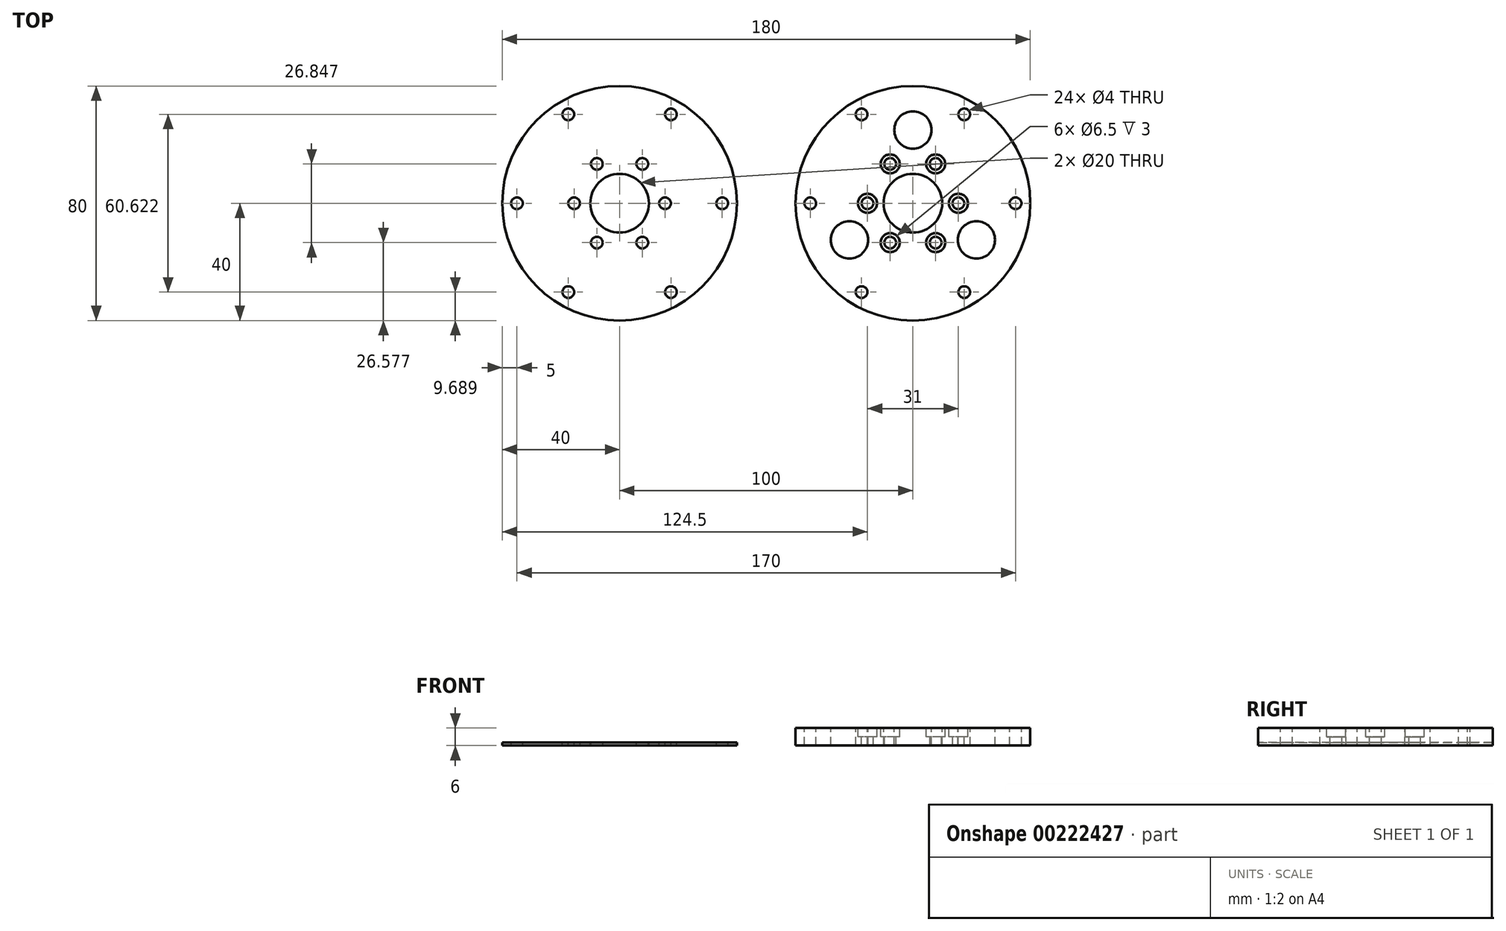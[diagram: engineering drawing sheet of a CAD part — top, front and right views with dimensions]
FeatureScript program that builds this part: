
annotation { "Feature Type Name" : "Feature", "Feature Type Description" : "" }
export const myFeature = defineFeature(function(context is Context, id is Id, definition is map)
    precondition{}
    {
        {
            var Q0;
            Q0=qCreatedBy(makeId("Top.planeOp"),FACE);
            var sketch = newSketch(context, id + "F0", { "sketchPlane" : qUnion([Q0])});
            skCircle(sketch, "E0", {"center": v(0, 0) * mm, "radius": 30 * mm});
            skCircle(sketch, "E1", {"center": v(0, 0) * mm, "radius": 40 * mm});
            skPoint(sketch, "E2", {"position": v(15.5, 0) * mm});
            skPoint(sketch, "E3.1.0", {"position": v(7.75, 13.42) * mm});
            skPoint(sketch, "E3.2.0", {"position": v(-7.75, 13.42) * mm});
            skPoint(sketch, "E3.3.0", {"position": v(-15.5, 0) * mm});
            skPoint(sketch, "E3.4.0", {"position": v(-7.75, -13.42) * mm});
            skPoint(sketch, "E3.5.0", {"position": v(7.75, -13.42) * mm});
            skPoint(sketch, "E4", {"position": v(35, 0) * mm});
            skPoint(sketch, "E5.1.0", {"position": v(17.5, 30.31) * mm});
            skPoint(sketch, "E5.2.0", {"position": v(-17.5, 30.31) * mm});
            skPoint(sketch, "E5.3.0", {"position": v(-35, 0) * mm});
            skPoint(sketch, "E5.4.0", {"position": v(-17.5, -30.31) * mm});
            skPoint(sketch, "E5.5.0", {"position": v(17.5, -30.31) * mm});
            skSolve(sketch);
        }
        {
            var Q0;
            Q0=makeQuery(id+"F0.imprint","IMPRINT",FACE,{"disambiguationData":[TD([[makeQuery(id+"F0.imprint","IMPRINT",EDGE,{"derivedFrom":sQuery(id+"F0.wireOp",EDGE,"E0")}),-1.0]])]});
            var Q1;
            Q1=makeQuery(id+"F0.imprint","IMPRINT",FACE,{"disambiguationData":[TD([[makeQuery(id+"F0.imprint","IMPRINT",EDGE,{"derivedFrom":sQuery(id+"F0.wireOp",EDGE,"E0")}),1.0]])]});
            extrude(context, id + "F1", {"entities" : qUnion([Q0, Q1]), "oppositeDirection" : true, "depth" : 1 * mm});
        }
        {
            var Q0;
            Q0=sQuery(id+"F0.wireOp",VERTEX,"E4");
            var Q1;
            Q1=sQuery(id+"F0.wireOp",VERTEX,"E5.1.0");
            var Q2;
            Q2=sQuery(id+"F0.wireOp",VERTEX,"E5.2.0");
            var Q3;
            Q3=sQuery(id+"F0.wireOp",VERTEX,"E5.3.0");
            var Q4;
            Q4=sQuery(id+"F0.wireOp",VERTEX,"E5.4.0");
            var Q5;
            Q5=sQuery(id+"F0.wireOp",VERTEX,"E5.5.0");
            var Q6;
            Q6=sQuery(id+"F0.wireOp",VERTEX,"E5.6.0");
            var Q7;
            Q7=sQuery(id+"F0.wireOp",VERTEX,"E5.7.0");
            var Q8;
            Q8=sQuery(id+"F0.wireOp",VERTEX,"E3.4.0");
            var Q9;
            Q9=sQuery(id+"F0.wireOp",VERTEX,"E3.5.0");
            var Q10;
            Q10=sQuery(id+"F0.wireOp",VERTEX,"E2");
            var Q11;
            Q11=sQuery(id+"F0.wireOp",VERTEX,"E3.1.0");
            var Q12;
            Q12=sQuery(id+"F0.wireOp",VERTEX,"E3.2.0");
            var Q13;
            Q13=sQuery(id+"F0.wireOp",VERTEX,"E3.3.0");
            var Q14;
            Q14=makeQuery(id+"F1.opExtrude","SWEPT_BODY",BODY,{"disambiguationData":[OSD([sQuery(id+"F0.wireOp",EDGE,"E1")])]});
            hole(context, id + "F2", {"style" : HoleStyle.SIMPLE, "endStyle" : HoleEndStyle.THROUGH, "standardTappedOrClearance" : lookupTablePath({ "standard" : "ISO", "fit" : "Normal", "engagement" : "75%", "pitch" : "1 mm", "size" : "M5", "type" : "Tapped" }), "standardBlindInLast" : lookupTablePath({ "fit" : "Standard", "standard" : "ISO", "engagement" : "75%", "pitch" : "1 mm", "size" : "M5", "type" : "Tapped" }), "holeDiameter" : 4 * mm, "locations" : qUnion([Q0, Q1, Q2, Q3, Q4, Q5, Q6, Q7, Q8, Q9, Q10, Q11, Q12, Q13]), "scope" : qUnion([Q14]), "isTappedThrough" : true, "showTappedDepth" : true});
        }
        {
            var Q0;
            Q0=sQuery(id+"F0.wireOp",VERTEX,"E0.center");
            var Q1;
            Q1=makeQuery(id+"F1.opExtrude","SWEPT_BODY",BODY,{"disambiguationData":[OSD([sQuery(id+"F0.wireOp",EDGE,"E1")])]});
            hole(context, id + "F3", {"style" : HoleStyle.SIMPLE, "endStyle" : HoleEndStyle.THROUGH, "holeDiameter" : 20 * mm, "locations" : qUnion([Q0]), "scope" : qUnion([Q1]), "isTappedThrough" : true});
        }
        {
            var Q0;
            Q0=makeQuery(id+"F1.opExtrude","SWEPT_BODY",BODY,{"disambiguationData":[OSD([sQuery(id+"F0.wireOp",EDGE,"E1")])]});
            transform(context, id + "F4", {"entities" : qUnion([Q0]), "transformType" : TransformType.TRANSLATION_3D, "dx" : 100 * mm, "dy" : 0 * mm, "dz" : 0 * mm, "makeCopy" : true});
        }
        {
            var Q0;
            Q0=makeQuery(id+"F4.opPattern","COPY",FACE,{"derivedFrom":makeQuery(id+"F1.opExtrude","CAP_FACE",FACE,{"disambiguationData":[OSD([sQuery(id+"F0.wireOp",EDGE,"E1")])],"isStart":true}),"instanceName":"1"});
            extrude(context, id + "F5", {"entities" : qUnion([Q0]), "operationType" : NewBodyOperationType.ADD, "depth" : 5 * mm});
        }
        {
            var Q0;
            Q0=makeQuery(id+"F5.opExtrude","CAP_FACE",FACE,{"disambiguationData":[OSD([sQuery(id+"F0.wireOp",EDGE,"E1")])],"isStart":false});
            var sketch = newSketch(context, id + "F6", { "sketchPlane" : qUnion([Q0])});
            skCircle(sketch, "E6.0", {"center": v(107.75, 13.42) * mm, "radius": 2.63 * mm, "construction": true});
            skCircle(sketch, "E7.0", {"center": v(100, 0) * mm, "radius": 10 * mm, "construction": true});
            skCircle(sketch, "E8.1.0", {"center": v(92.25, 13.42) * mm, "radius": 2.63 * mm, "construction": true});
            skCircle(sketch, "E8.2.0", {"center": v(84.5, 0) * mm, "radius": 2.63 * mm, "construction": true});
            skCircle(sketch, "E9.1.3.0", {"center": v(92.25, -13.42) * mm, "radius": 2.63 * mm, "construction": true});
            skCircle(sketch, "E9.1.4.0", {"center": v(107.75, -13.42) * mm, "radius": 2.63 * mm, "construction": true});
            skCircle(sketch, "E9.1.5.0", {"center": v(115.5, 0) * mm, "radius": 2.63 * mm, "construction": true});
            skSolve(sketch);
        }
        {
            var Q0;
            Q0=sQuery(id+"F6.wireOp",VERTEX,"E9.1.5.0.center");
            var Q1;
            Q1=sQuery(id+"F6.wireOp",VERTEX,"E9.1.4.0.center");
            var Q2;
            Q2=sQuery(id+"F6.wireOp",VERTEX,"E9.1.3.0.center");
            var Q3;
            Q3=sQuery(id+"F6.wireOp",VERTEX,"E8.2.0.center");
            var Q4;
            Q4=sQuery(id+"F6.wireOp",VERTEX,"E8.1.0.center");
            var Q5;
            Q5=sQuery(id+"F6.wireOp",VERTEX,"E6.0.center");
            var Q6;
            Q6=sQuery(id+"F6.wireOp",VERTEX,"E9.1.7.0.center");
            var Q7;
            Q7=sQuery(id+"F6.wireOp",VERTEX,"E9.1.6.0.center");
            var Q8;
            Q8=makeQuery(id+"F4.opPattern","COPY",BODY,{"derivedFrom":makeQuery(id+"F1.opExtrude","SWEPT_BODY",BODY,{"disambiguationData":[OSD([sQuery(id+"F0.wireOp",EDGE,"E1")])]}),"instanceName":"1"});
            hole(context, id + "F7", {"style" : HoleStyle.C_BORE, "endStyle" : HoleEndStyle.THROUGH, "standardTappedOrClearance" : lookupTablePath({ "standard" : "ISO", "fit" : "Close", "size" : "M3", "type" : "Clearance" }), "standardBlindInLast" : lookupTablePath({ "fit" : "Close", "standard" : "ISO", "size" : "M3", "type" : "Clearance" }), "holeDiameter" : 3.15 * mm, "cBoreDiameter" : 6.5 * mm, "cBoreDepth" : 3 * mm, "locations" : qUnion([Q0, Q1, Q2, Q3, Q4, Q5, Q6, Q7]), "scope" : qUnion([Q8]), "isTappedThrough" : true});
        }
        {
            var Q0;
            Q0=makeQuery(id+"F5.opExtrude","CAP_FACE",FACE,{"disambiguationData":[OSD([sQuery(id+"F0.wireOp",EDGE,"E1")])],"isStart":false});
            var sketch = newSketch(context, id + "F8", { "sketchPlane" : qUnion([Q0])});
            skCircle(sketch, "E10.0", {"center": v(100, 0) * mm, "radius": 10 * mm, "construction": true});
            skCircle(sketch, "E10.1", {"center": v(100, 0) * mm, "radius": 40 * mm, "construction": true});
            skLineSegment(sketch, "E11", {"start": v(140, 0) * mm, "end": v(100, 0) * mm, "construction": true});
            skLineSegment(sketch, "E12", {"start": v(100, 0) * mm, "end": v(134.64, -20) * mm, "construction": true});
            skPoint(sketch, "E13", {"position": v(121.65, -12.5) * mm});
            skPoint(sketch, "E14.1.0", {"position": v(100, 25) * mm});
            skPoint(sketch, "E14.2.0", {"position": v(78.35, -12.5) * mm});
            skSolve(sketch);
        }
        {
            var Q0;
            Q0=sQuery(id+"F8.wireOp",VERTEX,"E14.1.0");
            var Q1;
            Q1=sQuery(id+"F8.wireOp",VERTEX,"E13");
            var Q2;
            Q2=sQuery(id+"F8.wireOp",VERTEX,"E14.2.0");
            var Q3;
            Q3=makeQuery(id+"F4.opPattern","COPY",BODY,{"derivedFrom":makeQuery(id+"F1.opExtrude","SWEPT_BODY",BODY,{"disambiguationData":[OSD([sQuery(id+"F0.wireOp",EDGE,"E1")])]}),"instanceName":"1"});
            hole(context, id + "F9", {"style" : HoleStyle.SIMPLE, "endStyle" : HoleEndStyle.THROUGH, "holeDiameter" : 12.7 * mm, "locations" : qUnion([Q0, Q1, Q2]), "scope" : qUnion([Q3]), "isTappedThrough" : true});
        }
    });
